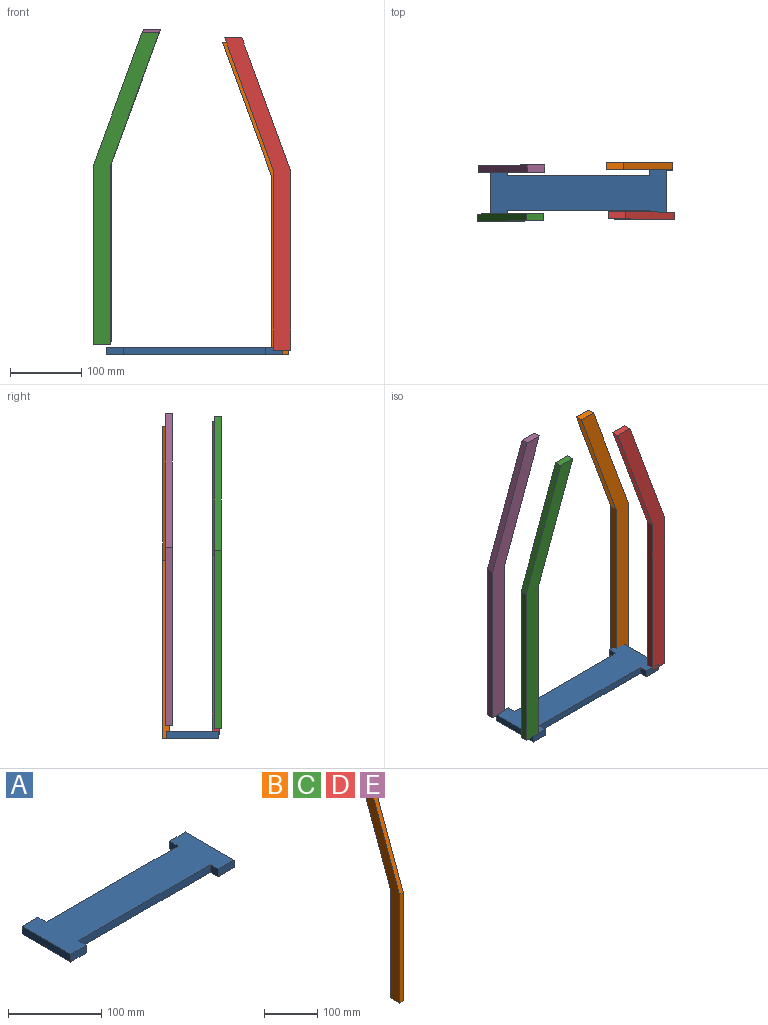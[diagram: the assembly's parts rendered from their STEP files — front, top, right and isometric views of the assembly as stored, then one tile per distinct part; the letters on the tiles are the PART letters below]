
ASSEMBLY  parts=5 mates=4
PART A: 14 faces, bbox 248x73.7x10 mm
  f0: plane 200x10mm, normal (0,-1,0), area 2000mm2, adj f1,f7,f8,f9
  f1: plane 11.96x10mm, normal (-1,0,0), area 119.6mm2, adj f0,f2,f7,f8
  f2: plane 24x10mm, normal (0,-1,0), area 240mm2, adj f1,f3,f7,f8
  f3: plane 73.71x10mm, normal (1,0,0), area 737.1mm2, adj f2,f4,f7,f8
  f4: plane 24x10mm, normal (0,1,0), area 240mm2, adj f3,f5,f7,f8
  f5: plane 12.93x10mm, normal (-1,0,0), area 129.3mm2, adj f4,f6,f7,f8
  f6: plane 200x10mm, normal (0,1,0), area 2000mm2, adj f5,f7,f8,f13
  f7: plane 248x73.71mm, normal (0,0,1), area 13300.7mm2, adj f0,f1,f2,f3,f4,f5,f6,f9
  f8: plane 248x73.71mm, normal (0,0,-1), area 13300.7mm2, adj f0,f1,f2,f3,f4,f5,f6,f9
  f9: plane 11.96x10mm, normal (1,0,0), area 119.6mm2, adj f0,f7,f8,f10
  f10: plane 24x10mm, normal (0,-1,0), area 240mm2, adj f7,f8,f9,f11
  f11: plane 73.71x10mm, normal (-1,0,0), area 737.1mm2, adj f7,f8,f10,f12
  f12: plane 24x10mm, normal (0,1,0), area 240mm2, adj f7,f8,f11,f13
  f13: plane 12.93x10mm, normal (1,0,0), area 129.3mm2, adj f6,f7,f8,f12
PART B: 8 faces, bbox 10x92.8x437.8 mm
  f0: plane 250x10mm, normal (0,-1,0), area 2500mm2, adj f1,f5,f6,f7
  f1: plane 24x10mm, normal (0,0,-1), area 240mm2, adj f0,f2,f6,f7
  f2: plane 250x10mm, normal (0,1,0), area 2500mm2, adj f1,f3,f6,f7
  f3: plane 187.81x68.76mm, normal (0,0.94,-0.34), area 2000mm2, adj f2,f4,f6,f7
  f4: plane 24x10mm, normal (0,0,1), area 240mm2, adj f3,f5,f6,f7
  f5: plane 187.81x68.76mm, normal (0,-0.94,0.34), area 2000mm2, adj f0,f4,f6,f7
  f6: plane 437.81x92.76mm, normal (1,0,0), area 10507.4mm2, adj f0,f1,f2,f3,f4,f5
  f7: plane 437.81x92.76mm, normal (-1,0,0), area 10507.4mm2, adj f0,f1,f2,f3,f4,f5
PART C: same geometry as B
PART D: same geometry as B
PART E: same geometry as B
PLACE A rot(axis=(0,1,0),180deg) t=(65.63,44.5,-17.32)mm
PLACE B rot(axis=(0,0,1),90deg) t=(-6.41,76.91,-27.54)mm
PLACE C rot(axis=(0,0,-1),90deg) t=(127.65,15,-13.82)mm
PLACE D rot(axis=(0,0,1),90deg) t=(-3.26,7.74,-21.52)mm
PLACE E rot(axis=(0,0,-1),90deg) t=(129.48,83.49,-9.92)mm
MATE parallel B.f6 <-> A.f12  axis (0,1,0) through (185.82,86.91,-27.54)mm
MATE parallel C.f7 <-> A.f2  axis (0,1,0) through (-64.58,15,-13.82)mm
MATE parallel D.f7 <-> A.f10  axis (0,-1,0) through (188.97,7.74,-21.52)mm
MATE parallel E.f7 <-> A.f4  axis (0,1,0) through (-62.75,83.49,-9.92)mm
